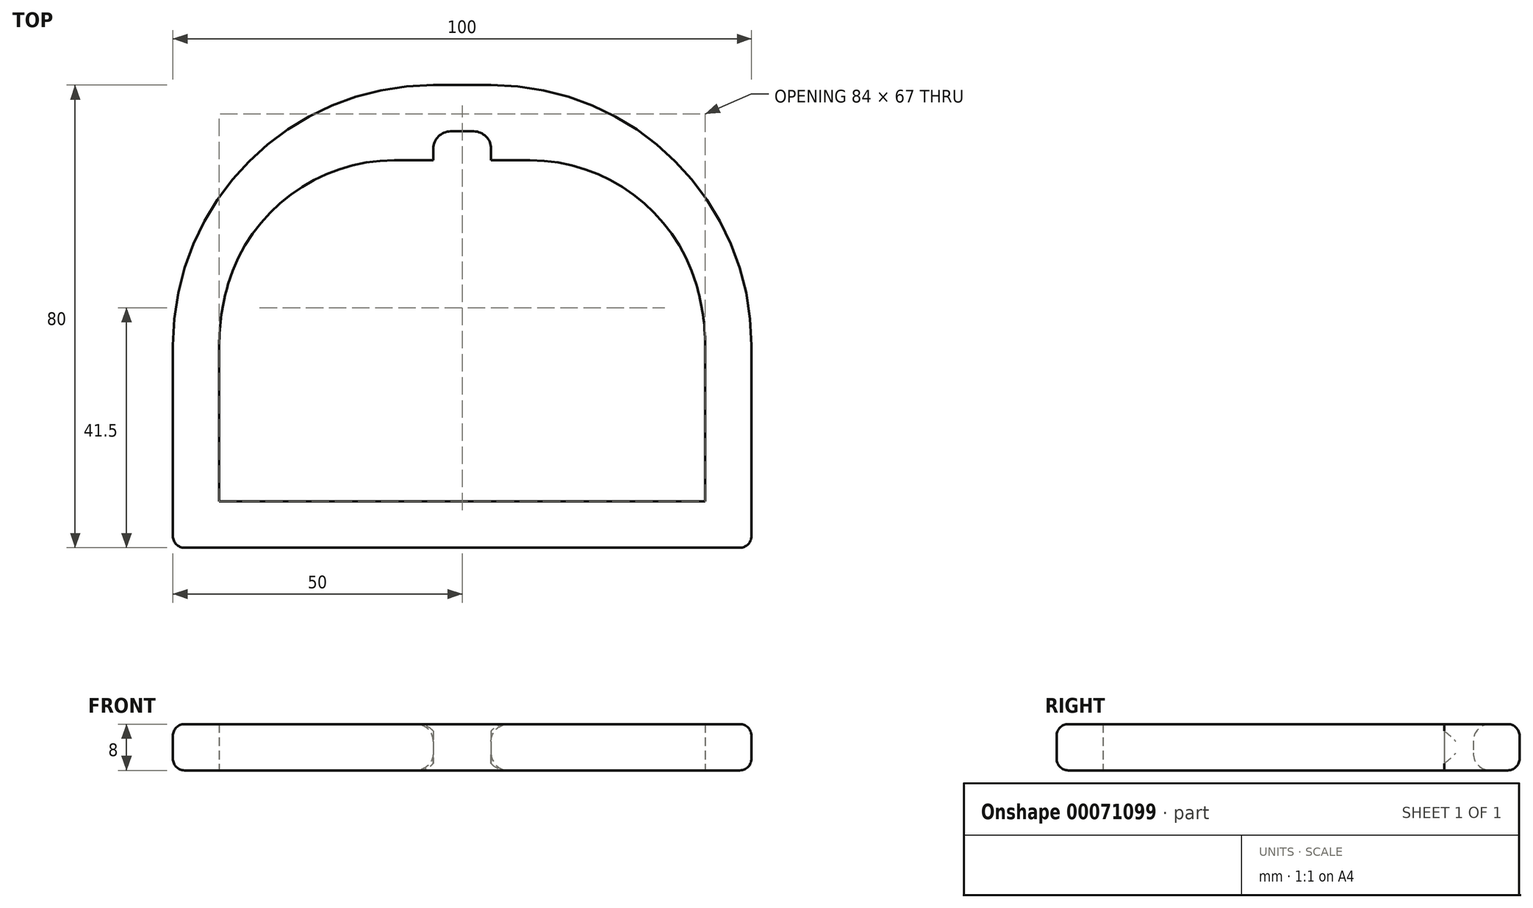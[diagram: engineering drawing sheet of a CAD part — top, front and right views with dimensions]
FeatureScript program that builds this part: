
annotation { "Feature Type Name" : "Feature", "Feature Type Description" : "" }
export const myFeature = defineFeature(function(context is Context, id is Id, definition is map)
    precondition{}
    {
        {
            var Q0;
            Q0=qCreatedBy(makeId("Top.planeOp"),FACE);
            var sketch = newSketch(context, id + "F0", { "sketchPlane" : qUnion([Q0])});
            skLineSegment(sketch, "E0.bottom", {"start": v(45, 0) * mm, "end": v(55, 0) * mm});
            skLineSegment(sketch, "E0.top", {"start": v(0, -80) * mm, "end": v(100, -80) * mm});
            skLineSegment(sketch, "E0.left", {"start": v(0, -45) * mm, "end": v(0, -80) * mm});
            skLineSegment(sketch, "E0.right", {"start": v(100, -45) * mm, "end": v(100, -80) * mm});
            skPoint(sketch, "E1.visualSharp", {"position": v(0, 0) * mm});
            skArc(sketch, "E1.filletArc", {"start": v(45, 0) * mm, "mid": v(13.18, -13.18) * mm, "end": v(0, -45) * mm});
            skPoint(sketch, "E2.visualSharp", {"position": v(100, 0) * mm});
            skArc(sketch, "E2.filletArc", {"start": v(100, -45) * mm, "mid": v(86.82, -13.18) * mm, "end": v(55, 0) * mm});
            skLineSegment(sketch, "E3.0", {"start": v(45, -8) * mm, "end": v(55, -8) * mm});
            skLineSegment(sketch, "E3.1", {"start": v(8, -45) * mm, "end": v(8, -72) * mm});
            skLineSegment(sketch, "E3.2", {"start": v(8, -72) * mm, "end": v(92, -72) * mm});
            skArc(sketch, "E3.3", {"start": v(9.54, -34.43) * mm, "mid": v(8.39, -39.66) * mm, "end": v(8, -45) * mm});
            skLineSegment(sketch, "E3.4", {"start": v(92, -45) * mm, "end": v(92, -72) * mm});
            skArc(sketch, "E3.5", {"start": v(92, -45) * mm, "mid": v(91.61, -39.66) * mm, "end": v(90.46, -34.43) * mm});
            skLineSegment(sketch, "E4", {"start": v(45, -8) * mm, "end": v(45, -13) * mm});
            skLineSegment(sketch, "E5", {"start": v(45, -13) * mm, "end": v(38.3, -13) * mm});
            skLineSegment(sketch, "E6", {"start": v(55, -8) * mm, "end": v(55, -13) * mm});
            skLineSegment(sketch, "E7", {"start": v(55, -13) * mm, "end": v(61.7, -13) * mm});
            skArc(sketch, "E8.filletArc", {"start": v(38.3, -13) * mm, "mid": v(20.36, -18.95) * mm, "end": v(9.54, -34.43) * mm});
            skArc(sketch, "E9.filletArc", {"start": v(90.46, -34.43) * mm, "mid": v(79.64, -18.95) * mm, "end": v(61.7, -13) * mm});
            skSolve(sketch);
        }
        {
            var Q0;
            Q0=makeQuery(id+"F0.imprint","IMPRINT",FACE,{"disambiguationData":[TD([[makeQuery(id+"F0.imprint","IMPRINT",EDGE,{"derivedFrom":sQuery(id+"F0.wireOp",EDGE,"E0.bottom")}),-1.0]])]});
            var Q1;
            {var subQ0=sQuery(id+"F0.wireOp",EDGE,"E6");Q1=makeQuery(id+"F0.imprint","IMPRINT",FACE,{"disambiguationData":[TD([[makeQuery(id+"F0.imprint","IMPRINT",EDGE,{"derivedFrom":subQ0}),1.0]])]});}
            var Q2;
            {var subQ0=sQuery(id+"F0.wireOp",EDGE,"E4");Q2=makeQuery(id+"F0.imprint","IMPRINT",FACE,{"disambiguationData":[TD([[makeQuery(id+"F0.imprint","IMPRINT",EDGE,{"derivedFrom":subQ0}),-1.0]])]});}
            extrude(context, id + "F1", {"entities" : qUnion([Q0, Q1, Q2]), "depth" : 8 * mm});
        }
        {
            var Q0;
            Q0=makeQuery(id+"F1.opExtrude","SWEPT_EDGE",EDGE,{"disambiguationData":[OSD([sQuery(id+"F0.wireOp",EDGE,"E0.top"),sQuery(id+"F0.wireOp",EDGE,"E0.left")])]});
            var Q1;
            Q1=makeQuery(id+"F1.opExtrude","SWEPT_EDGE",EDGE,{"disambiguationData":[OSD([sQuery(id+"F0.wireOp",EDGE,"E0.top"),sQuery(id+"F0.wireOp",EDGE,"E0.right")])]});
            var Q2;
            Q2=makeQuery(id+"F1.opExtrude","CAP_EDGE",EDGE,{"disambiguationData":[OSD([sQuery(id+"F0.wireOp",EDGE,"E0.top")])],"isStart":false});
            var Q3;
            Q3=makeQuery(id+"F1.opExtrude","CAP_EDGE",EDGE,{"disambiguationData":[OSD([sQuery(id+"F0.wireOp",EDGE,"E0.left")])],"isStart":false});
            var Q4;
            Q4=makeQuery(id+"F1.opExtrude","CAP_EDGE",EDGE,{"disambiguationData":[OSD([sQuery(id+"F0.wireOp",EDGE,"E0.top")])],"isStart":true});
            var Q5;
            Q5=makeQuery(id+"F1.opExtrude","CAP_EDGE",EDGE,{"disambiguationData":[OSD([sQuery(id+"F0.wireOp",EDGE,"E2.filletArc")])],"isStart":true});
            fillet(context, id + "F2", {"entities" : qUnion([Q0, Q1, Q2, Q3, Q4, Q5]), "radius" : 2 * mm, "tangentPropagation" : true, "allowEdgeOverflow" : false});
        }
        {
            var Q0;
            Q0=makeQuery(id+"F1.opExtrude","SWEPT_FACE",FACE,{"disambiguationData":[OSD([sQuery(id+"F0.wireOp",EDGE,"E3.0")])]});
            fillet(context, id + "F3", {"entities" : qUnion([Q0]), "radius" : 3 * mm, "tangentPropagation" : true, "allowEdgeOverflow" : false});
        }
    });
